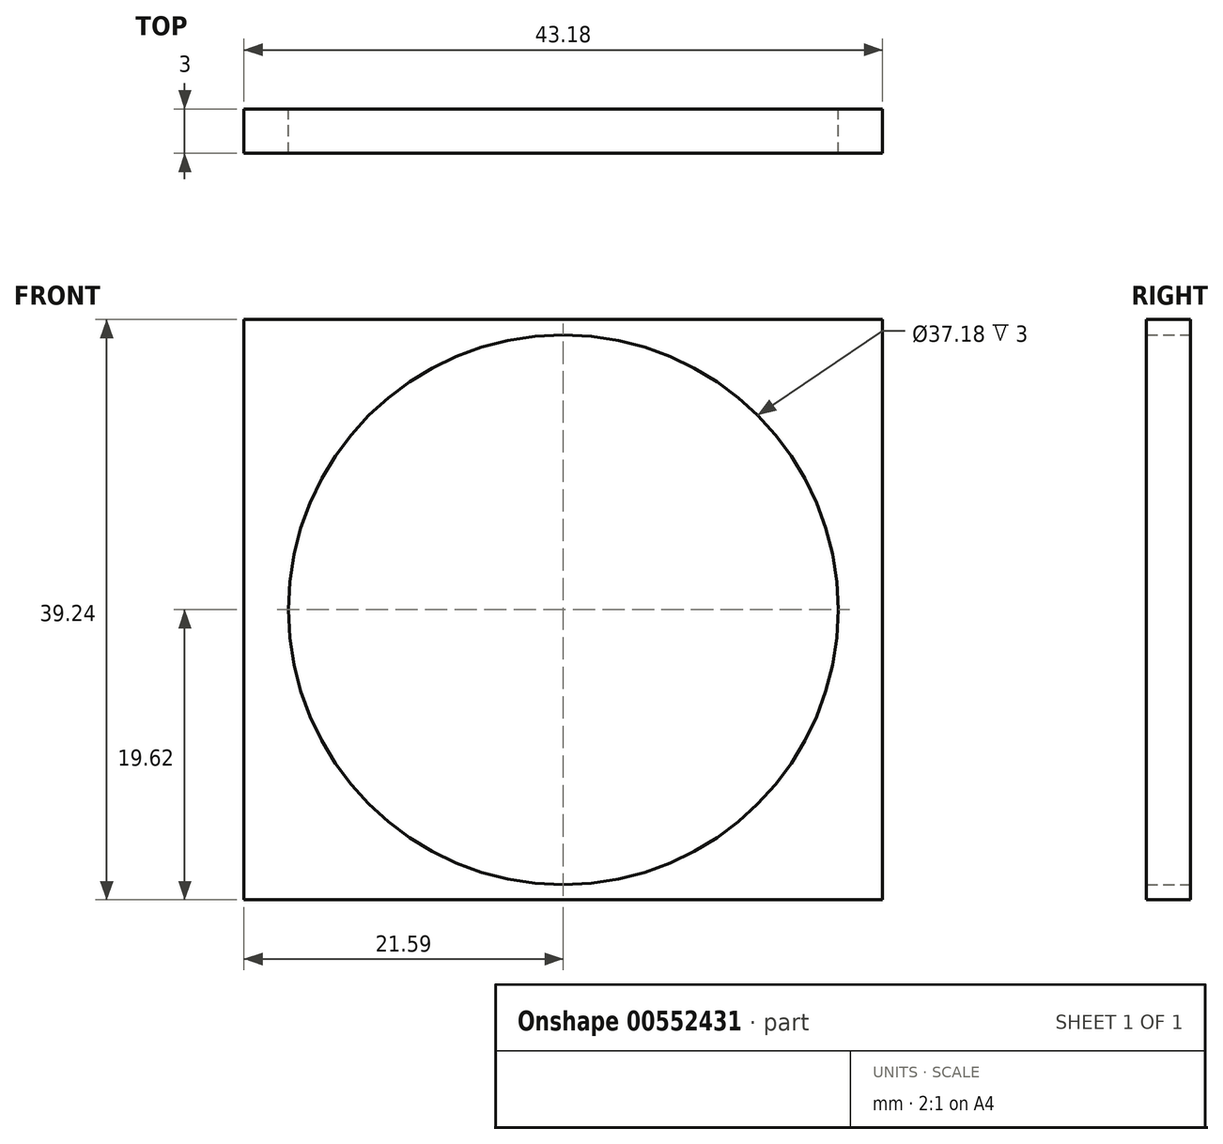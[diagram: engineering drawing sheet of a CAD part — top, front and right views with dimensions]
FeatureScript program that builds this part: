
annotation { "Feature Type Name" : "Feature", "Feature Type Description" : "" }
export const myFeature = defineFeature(function(context is Context, id is Id, definition is map)
    precondition{}
    {
        {
            var Q0;
            Q0=qCreatedBy(makeId("Front.planeOp"),FACE);
            var sketch = newSketch(context, id + "F0", { "sketchPlane" : qUnion([Q0])});
            skLineSegment(sketch, "E0.bottom", {"start": v(-21.59, 19.62) * mm, "end": v(21.6, 19.62) * mm});
            skLineSegment(sketch, "E0.top", {"start": v(-21.6, -19.62) * mm, "end": v(21.59, -19.62) * mm});
            skLineSegment(sketch, "E0.left", {"start": v(-21.59, 19.62) * mm, "end": v(-21.59, -19.62) * mm});
            skLineSegment(sketch, "E0.right", {"start": v(21.6, 19.62) * mm, "end": v(21.59, -19.62) * mm});
            skPoint(sketch, "E0.middle", {"position": v(0, 0) * mm});
            skCircle(sketch, "E1", {"center": v(0, 0) * mm, "radius": 18.59 * mm});
            skSolve(sketch);
        }
        {
            var Q0;
            Q0=makeQuery(id+"F0.imprint","IMPRINT",FACE,{"disambiguationData":[TD([[makeQuery(id+"F0.imprint","IMPRINT",EDGE,{"derivedFrom":sQuery(id+"F0.wireOp",EDGE,"E0.bottom")}),-1.0]])]});
            extrude(context, id + "F1", {"entities" : qUnion([Q0]), "depth" : 3 * mm, "offsetDistance" : 25.4 * mm});
        }
    });
